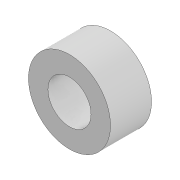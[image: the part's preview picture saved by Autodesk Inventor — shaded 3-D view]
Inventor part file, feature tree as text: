
AUTODESK INVENTOR PART (.ipt)
format: ipt  version: 2022 (Build 260153000, 153)  size: 84,480 bytes
history: native  units: mm
features: other x1, extrude x1, sketch x1
ambient origin geometry x8: Origin, YZ Plane, XZ Plane, XY Plane, X Axis, Y Axis, Z Axis, Center Point
bodies: Body1 (feature_tree)
feature tree (3):
  other  "Sólido1"
  extrude  "Extrusión1"  Depth=4.0mm
  sketch  "Boceto1"  dims[d0=8.0mm d1=4.2mm d2=4.0mm d3=0.0mm]
